# Revit family: Shower-Valve_Trim-KALLISTA-Vice-P34868
name_source: partatom
category: Specialty Equipment
units: mm (PartAtom-declared; Revit-internal decimal feet)

## family parameters
Cut with Voids When Loaded = No
Host = Face
OmniClass Number = 23.31.25.00
OmniClass Title = Toilet and Bath Specialties
Part Type = Normal
Room Calculation Point = No
Round Connector Dimension = Use Diameter
Shared = No

## types (5) — shared parameters
ADA Compliant = No
Assembly Code = C1030200
Date Modified = 05/23/2024
Default Elevation = 42"
Description = Transfer Trim Crank
Handle Clearance = 3 1/4"
Height = 4"
Length = 5 5/16"
Manufacturer = Kallista Co.
Master Format 2014 = 10 28 00
Master Format 2014 Name = Toilet, Bath, and Laundry Accessories
Material = Premium Metal Construction
Product Name = Vice
URL = https://www.kallista.com
WaterSense Certified = No
Width = 4"

## per-type parameters (varying)
| type | Finish | Model | Secondary Finish | Type |
| Bruhsed French Gold, AF-French Gold | Kallista-Metal-AF-French_Gold | P34868-BAF-AF | Kallista-Metal-BAF-Brushed_French_Gold | 1 |
| Bruhsed Bronze, CP-Chrome | Kallista-Metal-CP-Chrome | P34868-BV-CP | Kallista-Metal-BV-Brushed_Bronze | 4 |
| Chrome, CP-Chrome | Kallista-Metal-CP-Chrome | P34868-CP-CP | Kallista-Metal-CP-Chrome | 5 |
| Vibrant Bruhsed Nickel, BGP | Kallista-Metal-BGP | P34868-BN-BGP | Kallista-Metal-BN-Brushed_Nickel | 2 |
| Vibrant Bruhsed Nickel, SN-Polished Nickel | Kallista-Metal-SN-Polished_Nickel | P34868-BN-SN | Kallista-Metal-BN-Brushed_Nickel | 3 |

## geometry (parser evidence)
native form markers: Sweep x4
no freeform markers — native parametric forms only
